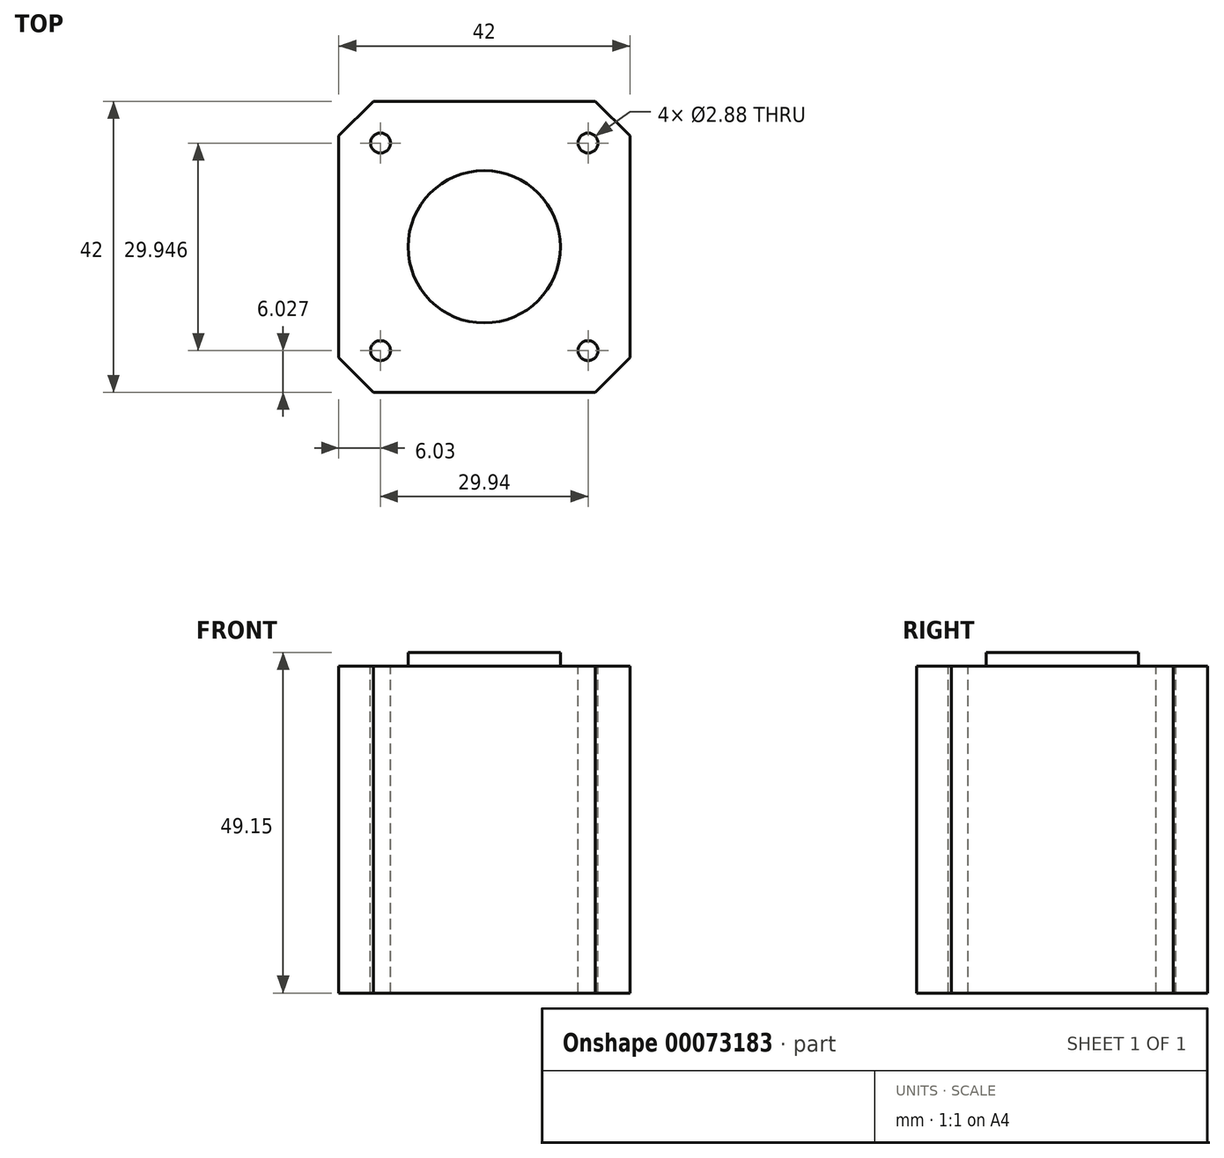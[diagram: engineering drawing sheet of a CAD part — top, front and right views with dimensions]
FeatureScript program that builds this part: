
annotation { "Feature Type Name" : "Feature", "Feature Type Description" : "" }
export const myFeature = defineFeature(function(context is Context, id is Id, definition is map)
    precondition{}
    {
        {
            var Q0;
            Q0=qCreatedBy(makeId("Top.planeOp"),FACE);
            var sketch = newSketch(context, id + "F0", { "sketchPlane" : qUnion([Q0])});
            skLineSegment(sketch, "E0.bottom", {"start": v(-21, 21) * mm, "end": v(21, 21) * mm});
            skLineSegment(sketch, "E0.top", {"start": v(-21, -21) * mm, "end": v(21, -21) * mm});
            skLineSegment(sketch, "E0.left", {"start": v(-21, 21) * mm, "end": v(-21, -21) * mm});
            skLineSegment(sketch, "E0.right", {"start": v(21, 21) * mm, "end": v(21, -21) * mm});
            skSolve(sketch);
        }
        {
            var Q0;
            Q0 = qSketchRegion(id + "F0", true);
            extrude(context, id + "F1", {"entities" : qUnion([Q0]), "depth" : 47.15 * mm});
        }
        {
            var Q0;
            Q0=makeQuery(id+"F1.opExtrude","SWEPT_EDGE",EDGE,{"disambiguationData":[OSD([sQuery(id+"F0.wireOp",EDGE,"E0.bottom"),sQuery(id+"F0.wireOp",EDGE,"E0.left")])]});
            var Q1;
            Q1=makeQuery(id+"F1.opExtrude","SWEPT_EDGE",EDGE,{"disambiguationData":[OSD([sQuery(id+"F0.wireOp",EDGE,"E0.top"),sQuery(id+"F0.wireOp",EDGE,"E0.left")])]});
            var Q2;
            Q2=makeQuery(id+"F1.opExtrude","SWEPT_EDGE",EDGE,{"disambiguationData":[OSD([sQuery(id+"F0.wireOp",EDGE,"E0.top"),sQuery(id+"F0.wireOp",EDGE,"E0.right")])]});
            var Q3;
            Q3=makeQuery(id+"F1.opExtrude","SWEPT_EDGE",EDGE,{"disambiguationData":[OSD([sQuery(id+"F0.wireOp",EDGE,"E0.bottom"),sQuery(id+"F0.wireOp",EDGE,"E0.right")])]});
            chamfer(context, id + "F2", {"entities" : qUnion([Q0, Q1, Q2, Q3]), "width" : 5 * mm, "tangentPropagation" : true});
        }
        {
            var Q0;
            Q0=makeQuery(id+"F1.opExtrude","CAP_FACE",FACE,{"disambiguationData":[OSD([sQuery(id+"F0.wireOp",EDGE,"E0.bottom"),sQuery(id+"F0.wireOp",EDGE,"E0.top"),sQuery(id+"F0.wireOp",EDGE,"E0.left"),sQuery(id+"F0.wireOp",EDGE,"E0.right")])],"isStart":false});
            var sketch = newSketch(context, id + "F3", { "sketchPlane" : qUnion([Q0])});
            skCircle(sketch, "E1", {"center": v(14.97, 14.97) * mm, "radius": 1.44 * mm});
            skCircle(sketch, "E2", {"center": v(14.97, -14.97) * mm, "radius": 1.44 * mm});
            skCircle(sketch, "E3", {"center": v(-14.97, -14.97) * mm, "radius": 1.44 * mm});
            skCircle(sketch, "E4", {"center": v(-14.97, 14.97) * mm, "radius": 1.44 * mm});
            skSolve(sketch);
        }
        {
            var Q0;
            Q0 = qSketchRegion(id + "F3", true);
            extrude(context, id + "F4", {"entities" : qUnion([Q0]), "operationType" : NewBodyOperationType.REMOVE, "endBound" : BoundingType.UP_TO_NEXT, "oppositeDirection" : true, "depth" : 25 * mm});
        }
        {
            var Q0;
            Q0=makeQuery(id+"F1.opExtrude","CAP_FACE",FACE,{"disambiguationData":[OSD([sQuery(id+"F0.wireOp",EDGE,"E0.bottom"),sQuery(id+"F0.wireOp",EDGE,"E0.top"),sQuery(id+"F0.wireOp",EDGE,"E0.left"),sQuery(id+"F0.wireOp",EDGE,"E0.right")])],"isStart":false});
            var sketch = newSketch(context, id + "F5", { "sketchPlane" : qUnion([Q0])});
            skCircle(sketch, "E5", {"center": v(0, 0) * mm, "radius": 11 * mm});
            skSolve(sketch);
        }
        {
            var Q0;
            Q0 = qSketchRegion(id + "F5", true);
            extrude(context, id + "F6", {"entities" : qUnion([Q0]), "operationType" : NewBodyOperationType.ADD, "depth" : 2 * mm});
        }
    });
